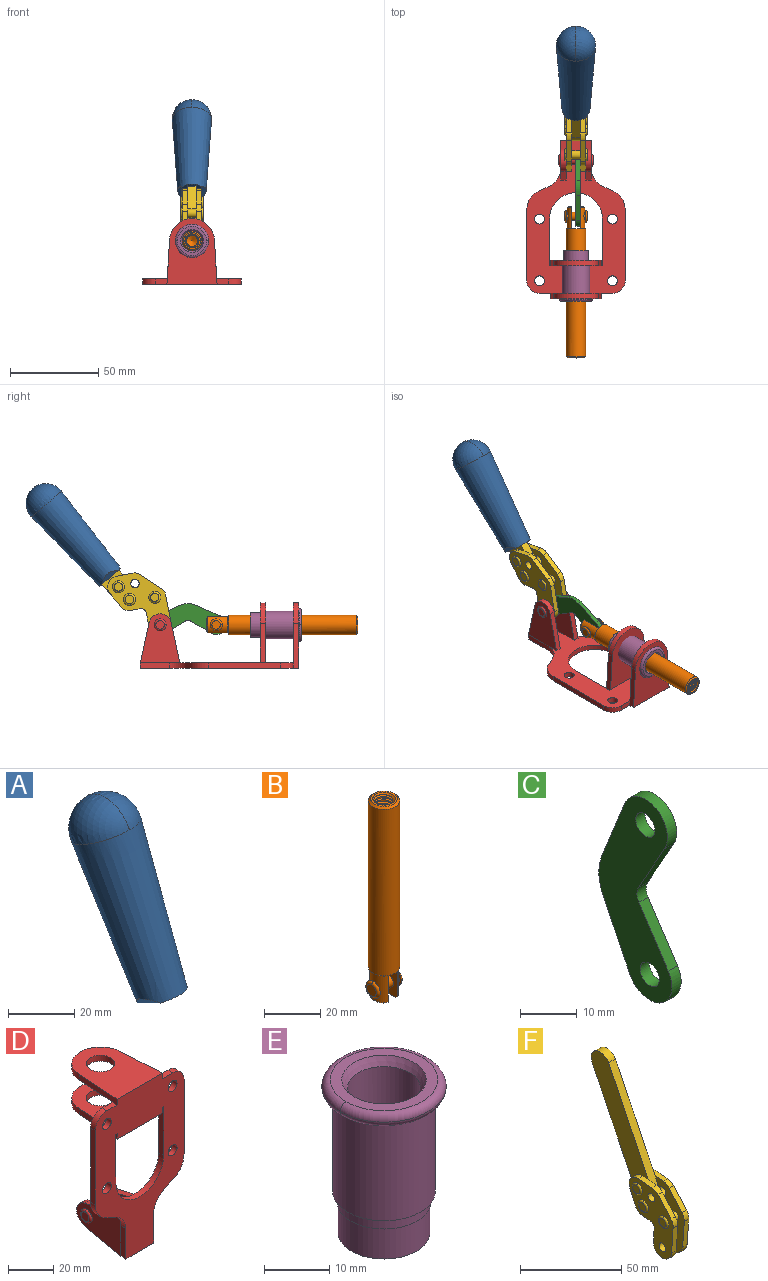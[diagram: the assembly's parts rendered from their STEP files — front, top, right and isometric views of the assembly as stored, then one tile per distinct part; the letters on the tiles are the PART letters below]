
ASSEMBLY  parts=6 mates=6
PART A: 11 faces, bbox 22.3x42.6x64.5 mm
  f0: sphere r=11.13mm, area 411.4mm2, adj f1,f8
  f1: cone r=11.11mm half-angle=3.3deg, axis (0,0.44,0.9), area 3251.8mm2, adj f0,f7,f8,f9,f10
  f2: cylinder r=6.16mm len=11.7mm, axis (1,0,0), area 89.5mm2, adj f3,f4,f5,f6
  f3: plane 60.23x36.75mm, normal (-1,0,0), area 763.6mm2, adj f2,f4,f6,f10
  f4: plane 51.37x25.05mm, normal (0,0.9,-0.44), area 264.2mm2, adj f2,f3,f5,f10
  f5: plane 60.23x36.75mm, normal (1,0,0), area 763.6mm2, adj f2,f4,f6,f10
  f6: plane 51.37x25.05mm, normal (0,-0.9,0.44), area 264.2mm2, adj f2,f3,f5,f10
  f7: plane 9.95x5.95mm, normal (0.71,-0.31,-0.64), area 25.8mm2, adj f1,f10
  f8: sphere r=11.13mm, area 411.4mm2, adj f0,f1
  f9: plane 9.95x5.95mm, normal (-0.71,-0.31,-0.64), area 25.8mm2, adj f1,f10
  f10: plane 14.27x11.38mm, normal (0,-0.44,-0.9), area 106.7mm2, adj f1,f3,f4,f5,f6,f7,f9
PART B: 48 faces, bbox 12.6x11.1x86.1 mm
  f0: torus R=2.41mm, axis (-1,0,0), area 15mm2, adj f30,f32,f34
  f1: torus R=2.41mm, axis (-1,0,0), area 15mm2, adj f29,f31,f33
  f2: cylinder r=5.54mm len=72.39mm, axis (0,0,1), area 2518.5mm2, adj f3,f4,f42,f43
  f3: cone r=5.54mm half-angle=45deg, axis (0,0,1), area 7.6mm2, adj f2,f5,f41
  f4: cone r=5.54mm half-angle=45deg, axis (0,0,-1), area 34.9mm2, adj f2,f39
  f5: cylinder r=5.08mm len=11.48mm, axis (0,0,1), area 108.3mm2, adj f3,f7,f8,f41
  f6: cylinder r=2.41mm len=4.83mm, axis (-1,0,0), area 71.2mm2, adj f40,f41
  f7: cylinder r=2.41mm len=4.83mm, axis (-1,0,0), area 7.6mm2, adj f5,f34
  f8: cone r=5.08mm half-angle=45deg, axis (0,0,1), area 10.6mm2, adj f5,f37,f41
  f9: cone r=3.98mm half-angle=45deg, axis (0,0,1), area 17.6mm2, adj f27,f39,f45,f46,f47
  f10: cylinder r=2.41mm len=4.83mm, axis (-1,0,0), area 7.6mm2, adj f33,f38
  f11: cylinder r=3.2mm len=6.4mm, axis (0,0,1), area 78.4mm2, adj f12,f28,f44,f45,f47
  f12: cylinder r=3.2mm len=6.4mm, axis (0,0,1), area 10.5mm2, adj f11,f13,f45,f47
  f13: cylinder r=3.2mm len=6.4mm, axis (0,0,1), area 10.5mm2, adj f12,f14,f45,f47
  f14: cylinder r=3.2mm len=6.4mm, axis (0,0,1), area 10.5mm2, adj f13,f15,f45,f47
  f15: cylinder r=3.2mm len=6.4mm, axis (0,0,1), area 10.5mm2, adj f14,f16,f45,f47
  f16: cylinder r=3.2mm len=6.4mm, axis (0,0,1), area 10.5mm2, adj f15,f17,f45,f47
  f17: cylinder r=3.2mm len=6.4mm, axis (0,0,1), area 10.5mm2, adj f16,f18,f45,f47
  f18: cylinder r=3.2mm len=6.4mm, axis (0,0,1), area 10.5mm2, adj f17,f19,f45,f47
  f19: cylinder r=3.2mm len=6.4mm, axis (0,0,1), area 10.5mm2, adj f18,f20,f45,f47
  f20: cylinder r=3.2mm len=6.4mm, axis (0,0,1), area 10.5mm2, adj f19,f21,f45,f47
  f21: cylinder r=3.2mm len=6.4mm, axis (0,0,1), area 10.5mm2, adj f20,f22,f45,f47
  f22: cylinder r=3.2mm len=6.4mm, axis (0,0,1), area 10.5mm2, adj f21,f23,f45,f47
  f23: cylinder r=3.2mm len=6.4mm, axis (0,0,1), area 10.5mm2, adj f22,f24,f45,f47
  f24: cylinder r=3.2mm len=6.4mm, axis (0,0,1), area 10.5mm2, adj f23,f25,f45,f47
  f25: cylinder r=3.2mm len=6.4mm, axis (0,0,1), area 10.5mm2, adj f24,f26,f45,f47
  f26: cylinder r=3.2mm len=6.4mm, axis (0,0,1), area 10.5mm2, adj f25,f27,f45,f47
  f27: cylinder r=3.2mm len=6.4mm, axis (0,0,1), area 7.4mm2, adj f9,f26,f45,f47
  f28: cone r=3.2mm half-angle=60deg, axis (0,0,1), area 37.2mm2, adj f11
  f29: plane 4.83x4.83mm, normal (-1,0,0), area 18.3mm2, adj f1,f31
  f30: plane 4.83x4.83mm, normal (1,0,0), area 18.3mm2, adj f0,f32
  f31: torus R=2.41mm, axis (-1,0,0), area 15mm2, adj f1,f29,f33
  f32: torus R=2.41mm, axis (-1,0,0), area 15mm2, adj f0,f30,f34
  f33: plane 6.83x6.83mm, normal (1,0,0), area 18.3mm2, adj f1,f10,f31
  f34: plane 6.83x6.83mm, normal (-1,0,0), area 18.3mm2, adj f0,f7,f32
  f35: cone r=5.08mm half-angle=45deg, axis (0,0,1), area 10.6mm2, adj f36,f38,f40
  f36: plane 7.25x1.97mm, normal (0,0,-1), area 10mm2, adj f35,f40
  f37: plane 7.25x1.97mm, normal (0,0,-1), area 10mm2, adj f8,f41
  f38: cylinder r=5.08mm len=11.48mm, axis (0,0,1), area 108.3mm2, adj f10,f35,f40,f42
  f39: plane 9.55x9.55mm, normal (0,0,1), area 22mm2, adj f4,f9
  f40: plane 12.76x10.09mm, normal (1,0,0), area 95.7mm2, adj f6,f35,f36,f38,f42,f43
  f41: plane 12.76x10.09mm, normal (-1,0,0), area 95.7mm2, adj f3,f5,f6,f8,f37,f43
  f42: cone r=5.54mm half-angle=45deg, axis (0,0,1), area 7.6mm2, adj f2,f38,f40
  f43: plane 11.07x4.7mm, normal (0,0,-1), area 50.4mm2, adj f2,f40,f41
  f44: plane 0.89x0.62mm, normal (-1,0,0), area 0.3mm2, adj f11,f45,f46,f47
  f45: bspline ~24.8x7.63mm, area 266.6mm2, adj f9,f11,f12,f13,f14,f15,f16,f17
  f46: bspline ~24.87x7.63mm, area 73.6mm2, adj f9,f44,f45,f47
  f47: bspline ~24.98x7.63mm, area 272.5mm2, adj f9,f11,f12,f13,f14,f15,f16,f17
PART C: 12 faces, bbox 2.3x18.2x42.8 mm
  f0: cylinder r=2.4mm len=4.8mm, axis (1,0,0), area 34.9mm2, adj f4,f11
  f1: cylinder r=10.41mm len=8.47mm, axis (1,0,0), area 20.2mm2, adj f4,f9,f10,f11
  f2: cylinder r=3.05mm len=3.16mm, axis (1,0,0), area 7.7mm2, adj f4,f6,f7,f11
  f3: cylinder r=2.4mm len=4.8mm, axis (1,0,0), area 34.9mm2, adj f4,f11
  f4: plane 42.81x18.23mm, normal (-1,0,0), area 414.1mm2, adj f0,f1,f2,f3,f5,f6,f7,f8
  f5: cylinder r=5.54mm len=10.67mm, axis (1,0,0), area 41.8mm2, adj f4,f6,f10,f11
  f6: plane 11.66x6.53mm, normal (0,-0.87,-0.49), area 30.9mm2, adj f2,f4,f5,f11
  f7: plane 11.17x7.33mm, normal (0,-0.84,0.55), area 30.9mm2, adj f2,f4,f8,f11
  f8: cylinder r=5.54mm len=10.51mm, axis (1,0,0), area 41.8mm2, adj f4,f7,f9,f11
  f9: plane 13.67x6.67mm, normal (0,0.9,-0.44), area 35.1mm2, adj f1,f4,f8,f11
  f10: plane 14.1x5.7mm, normal (0,0.93,0.37), area 35.1mm2, adj f1,f4,f5,f11
  f11: plane 42.81x18.23mm, normal (1,0,0), area 414.1mm2, adj f0,f1,f2,f3,f5,f6,f7,f8
PART D: 55 faces, bbox 55.7x37.4x89.8 mm
  f0: torus R=2.41mm, axis (-1,0,0), area 15mm2, adj f11,f15,f25
  f1: torus R=2.41mm, axis (-1,0,0), area 15mm2, adj f10,f12,f22
  f2: cylinder r=2.78mm len=5.56mm, axis (0,-1,0), area 54.2mm2, adj f30,f54
  f3: cylinder r=14.99mm len=29.97mm, axis (0,-1,0), area 145.9mm2, adj f30,f49,f53,f54
  f4: cylinder r=2.78mm len=5.56mm, axis (0,-1,0), area 54.2mm2, adj f30,f54
  f5: cylinder r=2.78mm len=5.56mm, axis (0,-1,0), area 54.2mm2, adj f30,f54
  f6: cylinder r=2.78mm len=5.56mm, axis (0,-1,0), area 54.2mm2, adj f30,f54
  f7: cylinder r=6.35mm len=12.7mm, axis (0,0,1), area 123.6mm2, adj f27,f51
  f8: cylinder r=6.35mm len=12.7mm, axis (0,0,-1), area 124.7mm2, adj f21,f35
  f9: cylinder r=2.41mm len=11.18mm, axis (-1,0,0), area 169.4mm2, adj f16,f19
  f10: plane 4.83x4.83mm, normal (1,0,0), area 18.3mm2, adj f1,f12
  f11: plane 4.83x4.83mm, normal (-1,0,0), area 18.3mm2, adj f0,f15
  f12: torus R=2.41mm, axis (-1,0,0), area 15mm2, adj f1,f10,f22
  f13: cylinder r=6.35mm len=12.41mm, axis (1,0,0), area 53.4mm2, adj f18,f19,f22,f23
  f14: cylinder r=6.35mm len=12.41mm, axis (-1,0,0), area 53.4mm2, adj f16,f17,f24,f25
  f15: torus R=2.41mm, axis (-1,0,0), area 15mm2, adj f0,f11,f25
  f16: plane 27.86x22.35mm, normal (1,0,0), area 425.4mm2, adj f9,f14,f17,f24,f30
  f17: plane 22.86x4.97mm, normal (0,0.21,0.98), area 72.5mm2, adj f14,f16,f25,f30
  f18: plane 22.86x4.97mm, normal (0,0.21,0.98), area 72.5mm2, adj f13,f19,f22,f30
  f19: plane 27.86x22.35mm, normal (-1,0,0), area 425.4mm2, adj f9,f13,f18,f23,f30
  f20: cylinder r=12.7mm len=25.35mm, axis (0,0,-1), area 119.8mm2, adj f21,f34,f35,f36
  f21: plane 34.21x28.07mm, normal (0,0,-1), area 702.4mm2, adj f8,f20,f30,f34,f36
  f22: plane 27.96x22.45mm, normal (1,0,0), area 407.2mm2, adj f1,f12,f13,f18,f23,f30,f42,f43
  f23: plane 22.86x4.97mm, normal (0,0.21,-0.98), area 72.5mm2, adj f13,f19,f22,f44
  f24: plane 22.86x4.97mm, normal (0,0.21,-0.98), area 72.5mm2, adj f14,f16,f25,f44
  f25: plane 27.86x22.35mm, normal (-1,0,0), area 407.1mm2, adj f0,f14,f15,f17,f24,f30,f45,f46
  f26: plane 3.1x0.95mm, normal (0,0,-1), area 2.7mm2, adj f30,f49,f50,f54
  f27: plane 34.21x28.07mm, normal (0,0,1), area 702.4mm2, adj f7,f28,f30,f50,f52
  f28: cylinder r=12.7mm len=25.35mm, axis (0,0,1), area 118.8mm2, adj f27,f50,f51,f52
  f29: plane 3.1x0.95mm, normal (0,0,-1), area 2.7mm2, adj f30,f52,f53,f54
  f30: plane 86.54x55.63mm, normal (0,1,0), area 2362.9mm2, adj f2,f3,f4,f5,f6,f16,f17,f18
  f31: plane 40.56x3.1mm, normal (-1,0,0), area 125.7mm2, adj f30,f32,f48,f54
  f32: cylinder r=7.11mm len=7.11mm, axis (0,-1,0), area 34.6mm2, adj f30,f31,f33,f54
  f33: plane 6.67x3.1mm, normal (0,0,1), area 20.4mm2, adj f30,f32,f34,f54
  f34: plane 25.39x3.13mm, normal (-1,0.06,0), area 79.5mm2, adj f20,f21,f33,f35,f54
  f35: plane 37.31x28.45mm, normal (0,0,1), area 789.9mm2, adj f8,f20,f34,f36,f54
  f36: plane 25.39x3.13mm, normal (1,0.06,0), area 79.5mm2, adj f20,f21,f35,f37,f54
  f37: plane 6.67x3.1mm, normal (0,0,1), area 20.4mm2, adj f30,f36,f38,f54
  f38: cylinder r=7.11mm len=7.11mm, axis (0,-1,0), area 34.6mm2, adj f30,f37,f39,f54
  f39: plane 40.56x3.1mm, normal (1,0,0), area 125.7mm2, adj f30,f38,f40,f54
  f40: cylinder r=11.18mm len=10.16mm, axis (0,-1,0), area 39.5mm2, adj f30,f39,f41,f54
  f41: plane 6.09x3.1mm, normal (0.42,0,-0.91), area 20.8mm2, adj f30,f40,f42,f54
  f42: cylinder r=11.18mm len=9.41mm, axis (0,-1,0), area 37.2mm2, adj f22,f30,f41,f43,f54
  f43: plane 16.5x3.1mm, normal (1,0,0), area 51.1mm2, adj f22,f42,f44,f54
  f44: plane 17.37x3.1mm, normal (0,0,-1), area 53.8mm2, adj f23,f24,f30,f43,f45,f54
  f45: plane 16.5x3.1mm, normal (-1,0,0), area 51.1mm2, adj f25,f44,f46,f54
  f46: cylinder r=11.18mm len=9.41mm, axis (0,-1,0), area 37.2mm2, adj f25,f30,f45,f47,f54
  f47: plane 6.09x3.1mm, normal (-0.42,0,-0.91), area 20.8mm2, adj f30,f46,f48,f54
  f48: cylinder r=11.18mm len=10.16mm, axis (0,-1,0), area 39.5mm2, adj f30,f31,f47,f54
  f49: plane 26.54x3.1mm, normal (-1,0,0), area 82.3mm2, adj f3,f26,f30,f54
  f50: plane 25.39x3.1mm, normal (1,0.06,0), area 78.8mm2, adj f26,f27,f28,f51,f54
  f51: plane 37.31x28.45mm, normal (0,0,-1), area 789.9mm2, adj f7,f28,f50,f52,f54
  f52: plane 25.39x3.1mm, normal (-1,0.06,0), area 78.8mm2, adj f27,f28,f29,f51,f54
  f53: plane 26.54x3.1mm, normal (1,0,0), area 82.3mm2, adj f3,f29,f30,f54
  f54: plane 89.66x55.63mm, normal (0,-1,0), area 2678.5mm2, adj f2,f3,f4,f5,f6,f26,f29,f31
PART E: 15 faces, bbox 20.6x20.6x28.7 mm
  f0: torus R=8.26mm, axis (0,0,1), area 56.8mm2, adj f1,f10,f12
  f1: torus R=8.26mm, axis (0,0,1), area 56.8mm2, adj f0,f6,f13
  f2: cylinder r=5.59mm len=25.91mm, axis (0,0,1), area 909.6mm2, adj f3,f4
  f3: cone r=6.86mm half-angle=45deg, axis (0,0,-1), area 70.2mm2, adj f2,f14
  f4: cone r=6.47mm half-angle=30deg, axis (0,0,1), area 66.7mm2, adj f2,f13
  f5: cylinder r=7.04mm len=14.07mm, axis (0,0,1), area 252.6mm2, adj f11,f14
  f6: torus R=8.26mm, axis (0,0,1), area 56.8mm2, adj f1,f12,f13
  f7: cylinder r=7.16mm len=14.33mm, axis (0,0,1), area 91.5mm2, adj f9,f11
  f8: cylinder r=7.86mm len=18.42mm, axis (0,0,1), area 909.6mm2, adj f9,f10
  f9: plane 15.72x15.72mm, normal (0,0,-1), area 33mm2, adj f7,f8
  f10: plane 16.51x16.51mm, normal (0,0,-1), area 19.9mm2, adj f0,f8,f12
  f11: plane 14.33x14.33mm, normal (0,0,-1), area 5.7mm2, adj f5,f7
  f12: torus R=8.26mm, axis (0,0,1), area 56.8mm2, adj f0,f6,f10
  f13: plane 16.51x16.51mm, normal (0,0,1), area 82.7mm2, adj f1,f4,f6
  f14: plane 14.07x14.07mm, normal (0,0,-1), area 7.8mm2, adj f3,f5
PART F: 59 faces, bbox 12.9x60.2x99.6 mm
  f0: torus R=2.39mm, axis (-1,0,0), area 14.9mm2, adj f20,f43,f51
  f1: torus R=2.39mm, axis (-1,0,0), area 14.9mm2, adj f19,f42,f51
  f2: torus R=2.39mm, axis (-1,0,0), area 14.9mm2, adj f18,f35,f51
  f3: torus R=2.39mm, axis (-1,0,0), area 14.9mm2, adj f14,f17,f23
  f4: torus R=2.39mm, axis (-1,0,0), area 14.9mm2, adj f13,f16,f23
  f5: torus R=2.39mm, axis (-1,0,0), area 14.9mm2, adj f12,f15,f23
  f6: cylinder r=2.39mm len=4.78mm, axis (1,0,0), area 46.5mm2, adj f48,f50,f51
  f7: cylinder r=2.39mm len=4.78mm, axis (1,0,0), area 46.5mm2, adj f50,f51
  f8: cylinder r=6.35mm len=12.68mm, axis (1,0,0), area 61.8mm2, adj f38,f39,f50,f51
  f9: cylinder r=2.39mm len=4.78mm, axis (-1,0,0), area 70.5mm2, adj f46,f50
  f10: cylinder r=2.39mm len=4.78mm, axis (-1,0,0), area 46.5mm2, adj f23,f45,f46
  f11: cylinder r=2.39mm len=4.78mm, axis (-1,0,0), area 46.5mm2, adj f23,f46
  f12: plane 4.78x4.78mm, normal (1,0,0), area 17.9mm2, adj f5,f15
  f13: plane 4.78x4.78mm, normal (1,0,0), area 17.9mm2, adj f4,f16
  f14: plane 4.78x4.78mm, normal (1,0,0), area 17.9mm2, adj f3,f17
  f15: torus R=2.39mm, axis (-1,0,0), area 14.9mm2, adj f5,f12,f23
  f16: torus R=2.39mm, axis (-1,0,0), area 14.9mm2, adj f4,f13,f23
  f17: torus R=2.39mm, axis (-1,0,0), area 14.9mm2, adj f3,f14,f23
  f18: plane 4.78x4.78mm, normal (-1,0,0), area 17.9mm2, adj f2,f35
  f19: plane 4.78x4.78mm, normal (-1,0,0), area 17.9mm2, adj f1,f42
  f20: plane 4.78x4.78mm, normal (-1,0,0), area 17.9mm2, adj f0,f43
  f21: plane 2.26x0.2mm, normal (1,0,0), area 0.2mm2, adj f31,f44
  f22: plane 2.26x0.2mm, normal (-1,0,0), area 0.2mm2, adj f41,f44
  f23: plane 39.37x30.77mm, normal (1,0,0), area 565.5mm2, adj f3,f4,f5,f10,f11,f15,f16,f17
  f24: cylinder r=6.1mm len=4.15mm, axis (-1,0,0), area 14.7mm2, adj f23,f25,f32,f46
  f25: plane 10.25x9.01mm, normal (0,-0.75,0.66), area 42.3mm2, adj f23,f24,f26,f46
  f26: cylinder r=6.35mm len=4.64mm, axis (-1,0,0), area 15.6mm2, adj f23,f25,f27,f46
  f27: plane 15.84x3.1mm, normal (0,-1,-0.07), area 49.2mm2, adj f23,f26,f28,f46
  f28: cylinder r=6.35mm len=12.68mm, axis (-1,0,0), area 61.8mm2, adj f23,f27,f29,f46
  f29: plane 8.11x3.1mm, normal (0,1,0.07), area 25.2mm2, adj f23,f28,f30,f46
  f30: cylinder r=3.05mm len=3.25mm, axis (-1,0,0), area 14.8mm2, adj f23,f29,f31,f46
  f31: plane 5.99x3.1mm, normal (0,0.07,-1), area 18.6mm2, adj f21,f23,f30,f44,f46
  f32: plane 9.5x3.1mm, normal (0,-0.07,1), area 29.5mm2, adj f23,f24,f33,f46,f47
  f33: cylinder r=6.1mm len=8.63mm, axis (-1,0,0), area 39.1mm2, adj f23,f32,f34,f47
  f34: plane 8.65x3.96mm, normal (0,0.91,-0.42), area 29.5mm2, adj f23,f33,f44,f47
  f35: torus R=2.39mm, axis (-1,0,0), area 14.9mm2, adj f2,f18,f51
  f36: plane 10.25x9.01mm, normal (0,-0.75,0.66), area 42.3mm2, adj f37,f49,f50,f51
  f37: cylinder r=6.35mm len=4.64mm, axis (1,0,0), area 15.6mm2, adj f36,f38,f50,f51
  f38: plane 15.84x3.1mm, normal (0,-1,-0.07), area 49.2mm2, adj f8,f37,f50,f51
  f39: plane 8.11x3.1mm, normal (0,1,0.07), area 25.2mm2, adj f8,f40,f50,f51
  f40: cylinder r=3.05mm len=3.25mm, axis (1,0,0), area 14.8mm2, adj f39,f41,f50,f51
  f41: plane 5.99x3.1mm, normal (0,0.07,-1), area 18.6mm2, adj f22,f40,f44,f50,f51
  f42: torus R=2.39mm, axis (-1,0,0), area 14.9mm2, adj f1,f19,f51
  f43: torus R=2.39mm, axis (-1,0,0), area 14.9mm2, adj f0,f20,f51
  f44: cylinder r=6.35mm len=12.12mm, axis (-1,0,0), area 128.9mm2, adj f21,f22,f23,f31,f34,f41,f46,f47
  f45: plane 2.65x1.35mm, normal (1,0,0), area 1mm2, adj f10,f55
  f46: plane 39.08x20.42mm, normal (-1,0,0), area 412.5mm2, adj f9,f10,f11,f24,f25,f26,f27,f28
  f47: plane 77.62x39.82mm, normal (1,0,0), area 850mm2, adj f32,f33,f34,f44,f53,f54,f55
  f48: plane 2.65x1.35mm, normal (-1,0,0), area 1mm2, adj f6,f55
  f49: cylinder r=6.1mm len=4.15mm, axis (1,0,0), area 14.7mm2, adj f36,f50,f51,f56
  f50: plane 39.08x20.42mm, normal (1,0,0), area 412.5mm2, adj f6,f7,f8,f9,f36,f37,f38,f39
  f51: plane 39.37x30.77mm, normal (-1,0,0), area 565.5mm2, adj f0,f1,f2,f6,f7,f8,f35,f36
  f52: plane 8.65x3.96mm, normal (0,0.91,-0.42), area 29.5mm2, adj f44,f51,f57,f58
  f53: plane 68.49x33.4mm, normal (0,0.9,-0.44), area 358.1mm2, adj f44,f47,f54,f58
  f54: cylinder r=6.35mm len=12.06mm, axis (1,0,0), area 93.7mm2, adj f47,f53,f55,f58
  f55: plane 68.49x33.4mm, normal (0,-0.9,0.44), area 358.1mm2, adj f44,f45,f46,f47,f48,f50,f54,f58
  f56: plane 9.5x3.1mm, normal (0,-0.07,1), area 29.5mm2, adj f49,f50,f51,f57,f58
  f57: cylinder r=6.1mm len=8.63mm, axis (1,0,0), area 39.1mm2, adj f51,f52,f56,f58
  f58: plane 77.62x39.82mm, normal (-1,0,0), area 850mm2, adj f44,f52,f53,f54,f55,f56,f57
PLACE A rot(axis=(-1,0,0),15deg) t=(-0.04,16.34,57.1)mm
PLACE B rot(axis=(1,0,0),90deg) t=(0,17.05,-3.1)mm
PLACE C rot(axis=(1,0,0),92deg) t=(1.16,17.9,-2.54)mm
PLACE D rot(axis=(1,0,0),90deg) t=(0,1.23,-3.1)mm fixed
PLACE E rot(axis=(1,0,0),90deg) t=(0,2.25,-3.1)mm
PLACE F rot(axis=(-1,0,0),15deg) t=(0,17.86,58.88)mm
MATE fastened F.f58 <-> A.f5  axis (-1,0,0) through (-2.35,81.98,71.89)mm
MATE fastened E.f2 <-> D.f7  axis (0,1,0) through (0,-45.16,21.51)mm
MATE slider B.f2 <-> E.f2  axis (0,-1,0) through (0,-41.73,21.51)mm
MATE revolute F.f7 <-> D.f0  axis (1,0,0) through (0,33.32,21.51)mm
MATE revolute C.f3 <-> D.f0  axis (1,0,0) through (0,33.32,21.51)mm
MATE revolute C.f0 <-> B.f6  axis (1,0,0) through (0,1.57,21.51)mm
